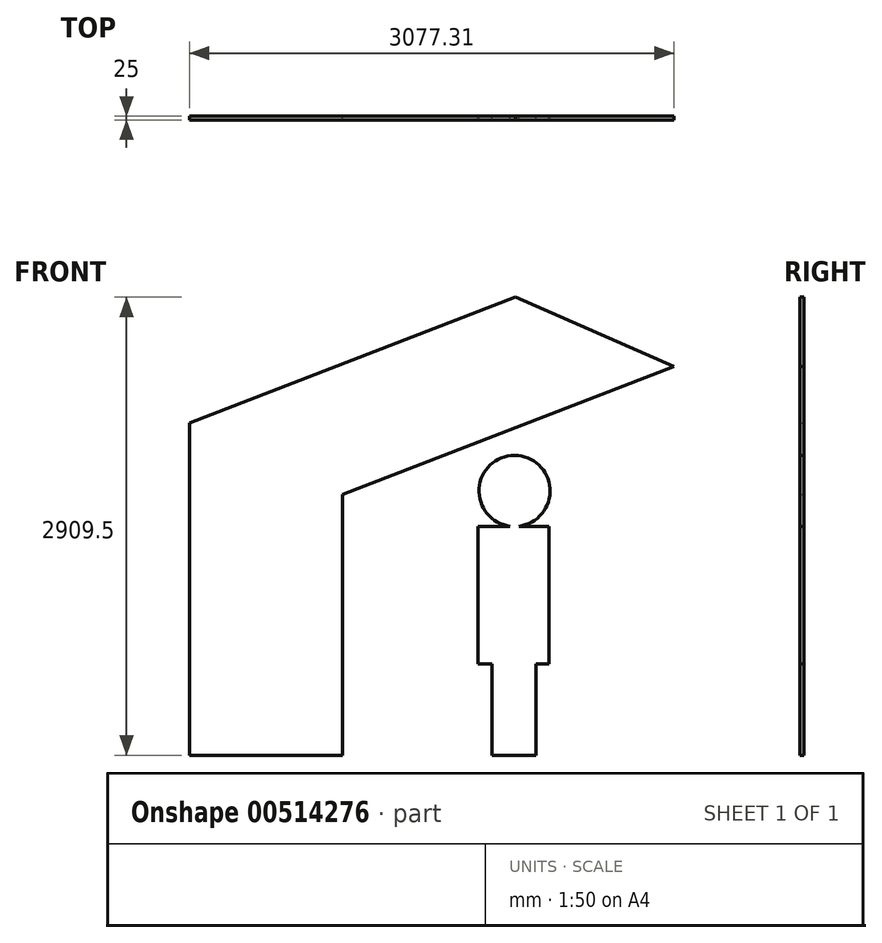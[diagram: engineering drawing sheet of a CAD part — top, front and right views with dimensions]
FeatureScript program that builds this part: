
annotation { "Feature Type Name" : "Feature", "Feature Type Description" : "" }
export const myFeature = defineFeature(function(context is Context, id is Id, definition is map)
    precondition{}
    {
        {
            var Q0;
            Q0=qCreatedBy(makeId("Front.planeOp"),FACE);
            var sketch = newSketch(context, id + "F0", { "sketchPlane" : qUnion([Q0])});
            skLineSegment(sketch, "E0.left", {"start": v(0, 0) * mm, "end": v(0, 1871.97) * mm});
            skLineSegment(sketch, "E1.bottom", {"start": v(339.8, 579.68) * mm, "end": v(621.98, 579.68) * mm});
            skLineSegment(sketch, "E1.top", {"start": v(339.8, 0) * mm, "end": v(621.98, 0) * mm});
            skLineSegment(sketch, "E1.left", {"start": v(339.8, 579.68) * mm, "end": v(339.8, 0) * mm});
            skLineSegment(sketch, "E1.right", {"start": v(621.98, 579.68) * mm, "end": v(621.98, 0) * mm});
            skLineSegment(sketch, "E2.bottom", {"start": v(252.97, 579.68) * mm, "end": v(701.57, 579.68) * mm});
            skLineSegment(sketch, "E2.top", {"start": v(252.97, 1455.17) * mm, "end": v(701.57, 1455.17) * mm});
            skLineSegment(sketch, "E2.left", {"start": v(252.97, 579.68) * mm, "end": v(252.97, 1455.17) * mm});
            skLineSegment(sketch, "E2.right", {"start": v(701.57, 579.68) * mm, "end": v(701.57, 1455.17) * mm});
            skCircle(sketch, "E3", {"center": v(484.5, 1679.47) * mm, "radius": 226.04 * mm});
            skSolve(sketch);
        }
        {
            var Q0;
            Q0=qCreatedBy(makeId("Front.planeOp"),FACE);
            var sketch = newSketch(context, id + "F1", { "sketchPlane" : qUnion([Q0])});
            skLineSegment(sketch, "E4", {"start": v(-608.05, 0) * mm, "end": v(-608.05, 1657.76) * mm});
            skLineSegment(sketch, "E5", {"start": v(-608.05, 1657.76) * mm, "end": v(1497.47, 2468.13) * mm});
            skLineSegment(sketch, "E6", {"start": v(1497.47, 2468.13) * mm, "end": v(491.74, 2909.5) * mm});
            skLineSegment(sketch, "E7", {"start": v(491.74, 2909.5) * mm, "end": v(-1579.84, 2112.19) * mm});
            skLineSegment(sketch, "E8", {"start": v(-1579.84, 2112.19) * mm, "end": v(-1579.84, 0) * mm});
            skLineSegment(sketch, "E9", {"start": v(-1579.84, 0) * mm, "end": v(-608.05, 0) * mm});
            skSolve(sketch);
        }
        {
            var Q0;
            Q0=makeQuery(id+"F1.imprint","IMPRINT",FACE,{"disambiguationData":[TD([[makeQuery(id+"F1.imprint","IMPRINT",EDGE,{"derivedFrom":sQuery(id+"F1.wireOp",EDGE,"E4")}),1.0]])]});
            extrude(context, id + "F2", {"entities" : qUnion([Q0]), "depth" : 25 * mm});
        }
        {
            var Q0;
            Q0 = qSketchRegion(id + "F0", true);
            extrude(context, id + "F3", {"entities" : qUnion([Q0]), "depth" : 25 * mm});
        }
    });
